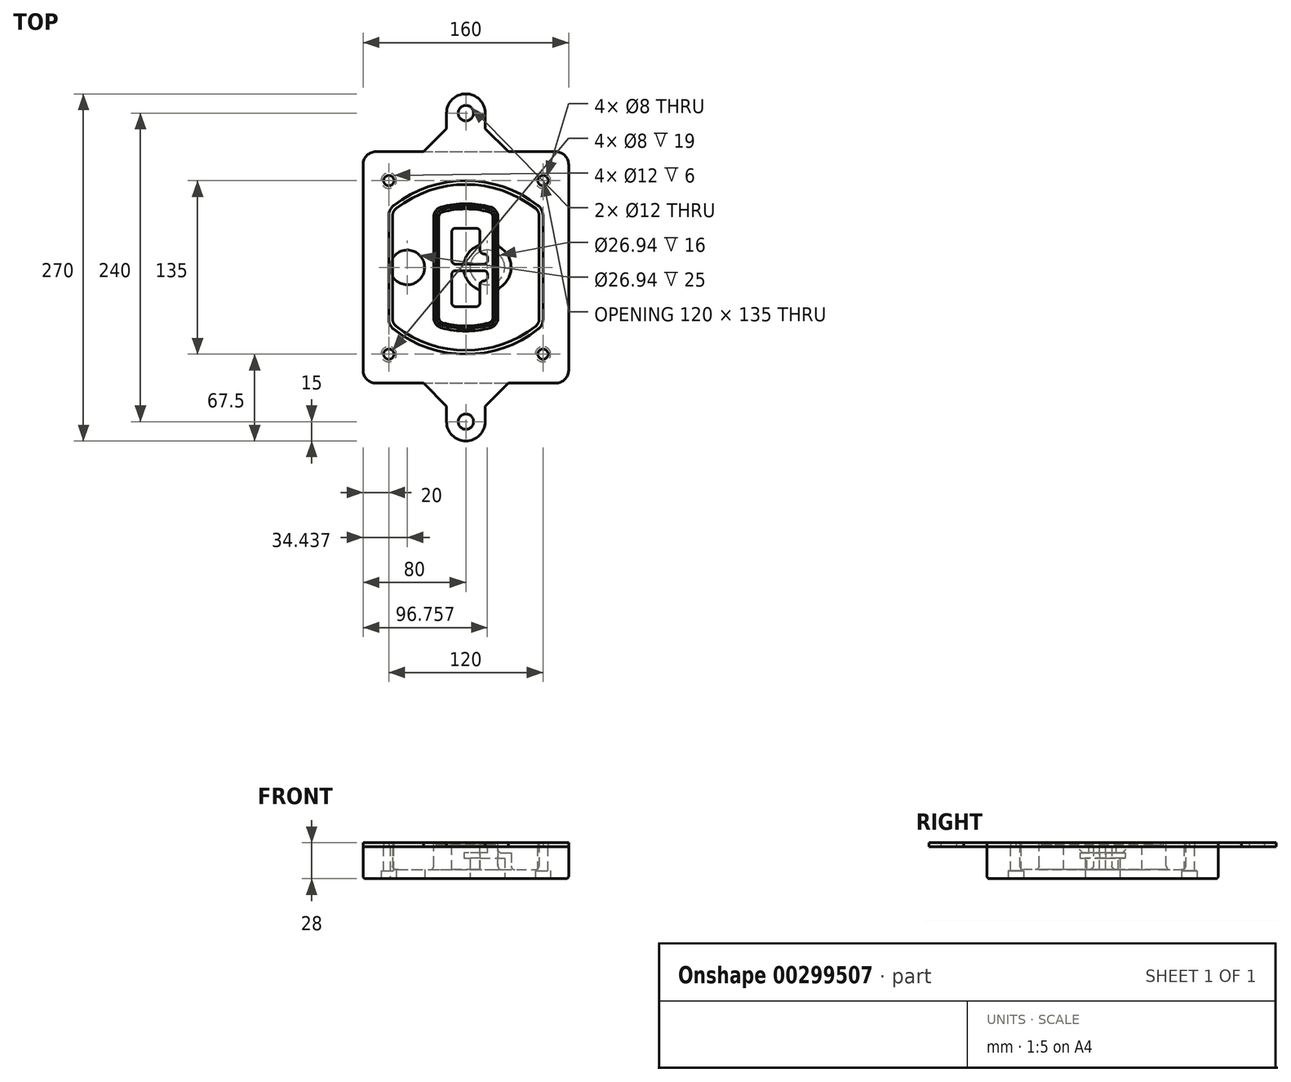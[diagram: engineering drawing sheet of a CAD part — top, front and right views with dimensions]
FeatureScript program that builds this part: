
annotation { "Feature Type Name" : "Feature", "Feature Type Description" : "" }
export const myFeature = defineFeature(function(context is Context, id is Id, definition is map)
    precondition{}
    {
        {
            var Q0;
            Q0=qCreatedBy(makeId("Top.planeOp"),FACE);
            var sketch = newSketch(context, id + "F0", { "sketchPlane" : qUnion([Q0])});
            skPoint(sketch, "E0.rect.middle", {"position": v(0, 0) * mm});
            skLineSegment(sketch, "E1.bottom", {"start": v(-70, -90) * mm, "end": v(70, -90) * mm});
            skLineSegment(sketch, "E1.top", {"start": v(-70, 90) * mm, "end": v(70, 90) * mm});
            skLineSegment(sketch, "E1.left", {"start": v(-80, -80) * mm, "end": v(-80, 80) * mm});
            skLineSegment(sketch, "E1.right", {"start": v(80, -80) * mm, "end": v(80, 80) * mm});
            skLineSegment(sketch, "E2", {"start": v(-80, 90) * mm, "end": v(80, -90) * mm, "construction": true});
            skLineSegment(sketch, "E3", {"start": v(80, 90) * mm, "end": v(-80, -90) * mm, "construction": true});
            skCircle(sketch, "E4", {"center": v(-60, 67.5) * mm, "radius": 4 * mm});
            skCircle(sketch, "E5", {"center": v(60, 67.5) * mm, "radius": 4 * mm});
            skCircle(sketch, "E6", {"center": v(60, -67.5) * mm, "radius": 4 * mm});
            skCircle(sketch, "E7", {"center": v(-60, -67.5) * mm, "radius": 4 * mm});
            skLineSegment(sketch, "E8", {"start": v(-60, 67.5) * mm, "end": v(60, 67.5) * mm, "construction": true});
            skLineSegment(sketch, "E9", {"start": v(60, 67.5) * mm, "end": v(60, -67.5) * mm, "construction": true});
            skLineSegment(sketch, "E10", {"start": v(60, -67.5) * mm, "end": v(-60, -67.5) * mm, "construction": true});
            skLineSegment(sketch, "E11", {"start": v(-60, -67.5) * mm, "end": v(-60, 67.5) * mm, "construction": true});
            skLineSegment(sketch, "E12", {"start": v(-60, 40.3) * mm, "end": v(-60, -40.3) * mm});
            skLineSegment(sketch, "E13", {"start": v(60, 40.3) * mm, "end": v(60, -40.3) * mm});
            skArc(sketch, "E14", {"start": v(56.15, 48.18) * mm, "mid": v(0, 67.5) * mm, "end": v(-56.15, 48.18) * mm});
            skArc(sketch, "E15", {"start": v(-56.15, -48.18) * mm, "mid": v(0, -67.5) * mm, "end": v(56.15, -48.18) * mm});
            skLineSegment(sketch, "E16", {"start": v(-60, 0) * mm, "end": v(60, 0) * mm, "construction": true});
            skPoint(sketch, "E17.visualSharp", {"position": v(-60, -45) * mm});
            skArc(sketch, "E17.filletArc", {"start": v(-60, -40.3) * mm, "mid": v(-58.99, -44.68) * mm, "end": v(-56.15, -48.18) * mm});
            skPoint(sketch, "E18.visualSharp", {"position": v(-60, 45) * mm});
            skArc(sketch, "E18.filletArc", {"start": v(-56.15, 48.18) * mm, "mid": v(-58.99, 44.68) * mm, "end": v(-60, 40.3) * mm});
            skPoint(sketch, "E19.visualSharp", {"position": v(60, 45) * mm});
            skArc(sketch, "E19.filletArc", {"start": v(60, 40.3) * mm, "mid": v(58.99, 44.68) * mm, "end": v(56.15, 48.18) * mm});
            skPoint(sketch, "E20.visualSharp", {"position": v(60, -45) * mm});
            skArc(sketch, "E20.filletArc", {"start": v(56.15, -48.18) * mm, "mid": v(58.99, -44.68) * mm, "end": v(60, -40.3) * mm});
            skPoint(sketch, "E21.visualSharp", {"position": v(-80, 90) * mm});
            skArc(sketch, "E21.filletArc", {"start": v(-70, 90) * mm, "mid": v(-77.07, 87.07) * mm, "end": v(-80, 80) * mm});
            skPoint(sketch, "E22.visualSharp", {"position": v(80, 90) * mm});
            skArc(sketch, "E22.filletArc", {"start": v(80, 80) * mm, "mid": v(77.07, 87.07) * mm, "end": v(70, 90) * mm});
            skPoint(sketch, "E23.visualSharp", {"position": v(80, -90) * mm});
            skArc(sketch, "E23.filletArc", {"start": v(70, -90) * mm, "mid": v(77.07, -87.07) * mm, "end": v(80, -80) * mm});
            skPoint(sketch, "E24.visualSharp", {"position": v(-80, -90) * mm});
            skArc(sketch, "E24.filletArc", {"start": v(-80, -80) * mm, "mid": v(-77.07, -87.07) * mm, "end": v(-70, -90) * mm});
            skArc(sketch, "E25.0", {"start": v(57, 40.3) * mm, "mid": v(56.3, 43.36) * mm, "end": v(54.3, 45.81) * mm});
            skLineSegment(sketch, "E25.1", {"start": v(57, 40.3) * mm, "end": v(57, -40.3) * mm});
            skArc(sketch, "E25.2", {"start": v(54.3, -45.81) * mm, "mid": v(56.3, -43.36) * mm, "end": v(57, -40.3) * mm});
            skArc(sketch, "E25.3", {"start": v(-54.3, -45.81) * mm, "mid": v(0, -64.5) * mm, "end": v(54.3, -45.81) * mm});
            skArc(sketch, "E25.4", {"start": v(-57, -40.3) * mm, "mid": v(-56.3, -43.36) * mm, "end": v(-54.3, -45.81) * mm});
            skArc(sketch, "E25.5", {"start": v(54.3, 45.81) * mm, "mid": v(0, 64.5) * mm, "end": v(-54.3, 45.81) * mm});
            skLineSegment(sketch, "E25.6", {"start": v(-57, 40.3) * mm, "end": v(-57, -40.3) * mm});
            skArc(sketch, "E25.7", {"start": v(-54.3, 45.81) * mm, "mid": v(-56.3, 43.36) * mm, "end": v(-57, 40.3) * mm});
            skArc(sketch, "E26.0", {"start": v(-58.62, 51.33) * mm, "mid": v(-62.58, 46.43) * mm, "end": v(-64, 40.3) * mm});
            skArc(sketch, "E26.1", {"start": v(58.62, 51.33) * mm, "mid": v(0, 71.5) * mm, "end": v(-58.62, 51.33) * mm});
            skArc(sketch, "E26.2", {"start": v(64, 40.3) * mm, "mid": v(62.58, 46.43) * mm, "end": v(58.62, 51.33) * mm});
            skLineSegment(sketch, "E26.3", {"start": v(64, 40.3) * mm, "end": v(64, -40.3) * mm});
            skArc(sketch, "E26.4", {"start": v(58.62, -51.33) * mm, "mid": v(62.58, -46.43) * mm, "end": v(64, -40.3) * mm});
            skLineSegment(sketch, "E26.5", {"start": v(-64, 40.3) * mm, "end": v(-64, -40.3) * mm});
            skArc(sketch, "E26.6", {"start": v(-58.62, -51.33) * mm, "mid": v(0, -71.5) * mm, "end": v(58.62, -51.33) * mm});
            skArc(sketch, "E26.7", {"start": v(-64, -40.3) * mm, "mid": v(-62.58, -46.43) * mm, "end": v(-58.62, -51.33) * mm});
            skSolve(sketch);
        }
        {
            var Q0;
            Q0=makeQuery(id+"F0.imprint","IMPRINT",FACE,{"disambiguationData":[TD([[makeQuery(id+"F0.imprint","IMPRINT",EDGE,{"derivedFrom":sQuery(id+"F0.wireOp",EDGE,"E1.bottom")}),1.0]])]});
            var Q1;
            Q1=makeQuery(id+"F0.imprint","IMPRINT",FACE,{"disambiguationData":[TD([[makeQuery(id+"F0.imprint","IMPRINT",EDGE,{"derivedFrom":sQuery(id+"F0.wireOp",EDGE,"E12")}),1.0]])]});
            var Q2;
            Q2=makeQuery(id+"F0.imprint","IMPRINT",FACE,{"disambiguationData":[TD([[makeQuery(id+"F0.imprint","IMPRINT",EDGE,{"derivedFrom":sQuery(id+"F0.wireOp",EDGE,"E25.0")}),1.0]])]});
            var Q3;
            Q3=makeQuery(id+"F0.imprint","IMPRINT",FACE,{"disambiguationData":[TD([[makeQuery(id+"F0.imprint","IMPRINT",EDGE,{"derivedFrom":sQuery(id+"F0.wireOp",EDGE,"E12")}),-1.0]])]});
            extrude(context, id + "F1", {"entities" : qUnion([Q0, Q1, Q2, Q3]), "oppositeDirection" : true, "depth" : 25 * mm});
        }
        {
            var Q0;
            Q0=makeQuery(id+"F0.imprint","IMPRINT",FACE,{"disambiguationData":[TD([[makeQuery(id+"F0.imprint","IMPRINT",EDGE,{"derivedFrom":sQuery(id+"F0.wireOp",EDGE,"E12")}),1.0]])]});
            extrude(context, id + "F2", {"entities" : qUnion([Q0]), "operationType" : NewBodyOperationType.ADD, "depth" : 3 * mm});
        }
        {
            var Q0;
            Q0=makeQuery(id+"F0.imprint","IMPRINT",FACE,{"disambiguationData":[TD([[makeQuery(id+"F0.imprint","IMPRINT",EDGE,{"derivedFrom":sQuery(id+"F0.wireOp",EDGE,"E25.0")}),1.0]])]});
            extrude(context, id + "F3", {"entities" : qUnion([Q0]), "operationType" : NewBodyOperationType.REMOVE, "oppositeDirection" : true, "depth" : 18 * mm});
        }
        {
            var Q0;
            Q0=makeQuery(id+"F2.opExtrude","CAP_FACE",FACE,{"disambiguationData":[OSD([sQuery(id+"F0.wireOp",EDGE,"E12"),sQuery(id+"F0.wireOp",EDGE,"E13"),sQuery(id+"F0.wireOp",EDGE,"E14"),sQuery(id+"F0.wireOp",EDGE,"E15"),sQuery(id+"F0.wireOp",EDGE,"E17.filletArc"),sQuery(id+"F0.wireOp",EDGE,"E18.filletArc"),sQuery(id+"F0.wireOp",EDGE,"E19.filletArc"),sQuery(id+"F0.wireOp",EDGE,"E20.filletArc"),sQuery(id+"F0.wireOp",EDGE,"E25.0"),sQuery(id+"F0.wireOp",EDGE,"E25.1"),sQuery(id+"F0.wireOp",EDGE,"E25.2"),sQuery(id+"F0.wireOp",EDGE,"E25.3"),sQuery(id+"F0.wireOp",EDGE,"E25.4"),sQuery(id+"F0.wireOp",EDGE,"E25.5"),sQuery(id+"F0.wireOp",EDGE,"E25.6"),sQuery(id+"F0.wireOp",EDGE,"E25.7")])],"isStart":false});
            var sketch = newSketch(context, id + "F4", { "sketchPlane" : qUnion([Q0])});
            skArc(sketch, "E27.0", {"start": v(-19.08, -46.97) * mm, "mid": v(0, -49.5) * mm, "end": v(19.08, -46.97) * mm});
            skArc(sketch, "E28.0", {"start": v(19.08, 46.97) * mm, "mid": v(0, 49.5) * mm, "end": v(-19.08, 46.97) * mm});
            skLineSegment(sketch, "E29", {"start": v(-25, 39.25) * mm, "end": v(-25, -39.25) * mm});
            skLineSegment(sketch, "E30", {"start": v(25, 39.25) * mm, "end": v(25, -39.25) * mm});
            skLineSegment(sketch, "E31", {"start": v(-25, 45.1) * mm, "end": v(25, 45.1) * mm, "construction": true});
            skLineSegment(sketch, "E32", {"start": v(-25, -45.1) * mm, "end": v(25, -45.1) * mm, "construction": true});
            skPoint(sketch, "E33.visualSharp", {"position": v(-25, 45.1) * mm});
            skArc(sketch, "E33.filletArc", {"start": v(-19.08, 46.97) * mm, "mid": v(-23.35, 44.11) * mm, "end": v(-25, 39.25) * mm});
            skPoint(sketch, "E34.visualSharp", {"position": v(25, 45.1) * mm});
            skArc(sketch, "E34.filletArc", {"start": v(25, 39.25) * mm, "mid": v(23.35, 44.11) * mm, "end": v(19.08, 46.97) * mm});
            skPoint(sketch, "E35.visualSharp", {"position": v(25, -45.1) * mm});
            skArc(sketch, "E35.filletArc", {"start": v(19.08, -46.97) * mm, "mid": v(23.35, -44.11) * mm, "end": v(25, -39.25) * mm});
            skPoint(sketch, "E36.visualSharp", {"position": v(-25, -45.1) * mm});
            skArc(sketch, "E36.filletArc", {"start": v(-25, -39.25) * mm, "mid": v(-23.35, -44.11) * mm, "end": v(-19.08, -46.97) * mm});
            skArc(sketch, "E37.0", {"start": v(54.3, 45.81) * mm, "mid": v(0, 64.5) * mm, "end": v(-54.3, 45.81) * mm});
            skArc(sketch, "E37.1", {"start": v(-54.3, 45.81) * mm, "mid": v(-56.3, 43.36) * mm, "end": v(-57, 40.3) * mm});
            skLineSegment(sketch, "E37.2", {"start": v(-57, 40.3) * mm, "end": v(-57, -40.3) * mm});
            skArc(sketch, "E37.3", {"start": v(-57, -40.3) * mm, "mid": v(-56.3, -43.36) * mm, "end": v(-54.3, -45.81) * mm});
            skArc(sketch, "E37.4", {"start": v(-54.3, -45.81) * mm, "mid": v(0, -64.5) * mm, "end": v(54.3, -45.81) * mm});
            skArc(sketch, "E37.5", {"start": v(54.3, -45.81) * mm, "mid": v(56.3, -43.36) * mm, "end": v(57, -40.3) * mm});
            skLineSegment(sketch, "E37.6", {"start": v(57, 40.3) * mm, "end": v(57, -40.3) * mm});
            skArc(sketch, "E37.7", {"start": v(57, 40.3) * mm, "mid": v(56.3, 43.36) * mm, "end": v(54.3, 45.81) * mm});
            skLineSegment(sketch, "E38.0", {"start": v(23, 39.25) * mm, "end": v(23, -39.25) * mm});
            skArc(sketch, "E38.1", {"start": v(18.56, -45.04) * mm, "mid": v(21.76, -42.9) * mm, "end": v(23, -39.25) * mm});
            skArc(sketch, "E38.2", {"start": v(-18.56, -45.04) * mm, "mid": v(0, -47.5) * mm, "end": v(18.56, -45.04) * mm});
            skArc(sketch, "E38.3", {"start": v(-23, -39.25) * mm, "mid": v(-21.76, -42.9) * mm, "end": v(-18.56, -45.04) * mm});
            skLineSegment(sketch, "E38.4", {"start": v(-23, 39.25) * mm, "end": v(-23, -39.25) * mm});
            skArc(sketch, "E38.5", {"start": v(23, 39.25) * mm, "mid": v(21.76, 42.9) * mm, "end": v(18.56, 45.04) * mm});
            skArc(sketch, "E38.6", {"start": v(-18.56, 45.04) * mm, "mid": v(-21.76, 42.9) * mm, "end": v(-23, 39.25) * mm});
            skArc(sketch, "E38.7", {"start": v(18.56, 45.04) * mm, "mid": v(0, 47.5) * mm, "end": v(-18.56, 45.04) * mm});
            skArc(sketch, "E39.0", {"start": v(21, 39.25) * mm, "mid": v(20.18, 41.68) * mm, "end": v(18.04, 43.1) * mm});
            skLineSegment(sketch, "E39.1", {"start": v(21, 39.25) * mm, "end": v(21, -39.25) * mm});
            skArc(sketch, "E39.2", {"start": v(18.04, -43.1) * mm, "mid": v(20.18, -41.68) * mm, "end": v(21, -39.25) * mm});
            skArc(sketch, "E39.3", {"start": v(-18.04, -43.1) * mm, "mid": v(0, -45.5) * mm, "end": v(18.04, -43.1) * mm});
            skArc(sketch, "E39.4", {"start": v(-21, -39.25) * mm, "mid": v(-20.18, -41.68) * mm, "end": v(-18.04, -43.1) * mm});
            skArc(sketch, "E39.5", {"start": v(18.04, 43.1) * mm, "mid": v(0, 45.5) * mm, "end": v(-18.04, 43.1) * mm});
            skLineSegment(sketch, "E39.6", {"start": v(-21, 39.25) * mm, "end": v(-21, -39.25) * mm});
            skArc(sketch, "E39.7", {"start": v(-18.04, 43.1) * mm, "mid": v(-20.18, 41.68) * mm, "end": v(-21, 39.25) * mm});
            skLineSegment(sketch, "E40", {"start": v(-25, 0) * mm, "end": v(25, 0) * mm, "construction": true});
            skLineSegment(sketch, "E41", {"start": v(-11, 5.5) * mm, "end": v(-11, 27.5) * mm});
            skLineSegment(sketch, "E42", {"start": v(-8, 30.5) * mm, "end": v(8, 30.5) * mm});
            skLineSegment(sketch, "E43", {"start": v(11, 27.5) * mm, "end": v(11, 13.5) * mm});
            skLineSegment(sketch, "E44", {"start": v(14, 10.5) * mm, "end": v(14, 10.5) * mm});
            skLineSegment(sketch, "E45", {"start": v(17, 7.5) * mm, "end": v(17, 5.5) * mm});
            skLineSegment(sketch, "E46", {"start": v(14, 2.5) * mm, "end": v(-8, 2.5) * mm});
            skPoint(sketch, "E47.visualSharp", {"position": v(-11, 30.5) * mm});
            skArc(sketch, "E47.filletArc", {"start": v(-8, 30.5) * mm, "mid": v(-10.12, 29.62) * mm, "end": v(-11, 27.5) * mm});
            skPoint(sketch, "E48.visualSharp", {"position": v(11, 30.5) * mm});
            skArc(sketch, "E48.filletArc", {"start": v(11, 27.5) * mm, "mid": v(10.12, 29.62) * mm, "end": v(8, 30.5) * mm});
            skPoint(sketch, "E49.visualSharp", {"position": v(11, 10.5) * mm});
            skArc(sketch, "E49.filletArc", {"start": v(11, 13.5) * mm, "mid": v(11.88, 11.38) * mm, "end": v(14, 10.5) * mm});
            skPoint(sketch, "E50.visualSharp", {"position": v(17, 10.5) * mm});
            skArc(sketch, "E50.filletArc", {"start": v(17, 7.5) * mm, "mid": v(16.12, 9.62) * mm, "end": v(14, 10.5) * mm});
            skPoint(sketch, "E51.visualSharp", {"position": v(17, 2.5) * mm});
            skArc(sketch, "E51.filletArc", {"start": v(14, 2.5) * mm, "mid": v(16.12, 3.38) * mm, "end": v(17, 5.5) * mm});
            skPoint(sketch, "E52.visualSharp", {"position": v(-11, 2.5) * mm});
            skArc(sketch, "E52.filletArc", {"start": v(-11, 5.5) * mm, "mid": v(-10.12, 3.38) * mm, "end": v(-8, 2.5) * mm});
            skLineSegment(sketch, "E53.0.MirrorCS", {"start": v(14, -2.5) * mm, "end": v(-8, -2.5) * mm});
            skArc(sketch, "E54.0.MirrorCS", {"start": v(-11, -5.5) * mm, "mid": v(-10.12, -3.38) * mm, "end": v(-8, -2.5) * mm});
            skLineSegment(sketch, "E55.0.MirrorCS", {"start": v(-11, -5.5) * mm, "end": v(-11, -27.5) * mm});
            skArc(sketch, "E56.0.MirrorCS", {"start": v(-8, -30.5) * mm, "mid": v(-10.12, -29.62) * mm, "end": v(-11, -27.5) * mm});
            skLineSegment(sketch, "E57.0.MirrorCS", {"start": v(-8, -30.5) * mm, "end": v(8, -30.5) * mm});
            skArc(sketch, "E58.0.MirrorCS", {"start": v(11, -27.5) * mm, "mid": v(10.12, -29.62) * mm, "end": v(8, -30.5) * mm});
            skLineSegment(sketch, "E59.0.MirrorCS", {"start": v(11, -27.5) * mm, "end": v(11, -13.5) * mm});
            skArc(sketch, "E60.0.MirrorCS", {"start": v(11, -13.5) * mm, "mid": v(11.88, -11.38) * mm, "end": v(14, -10.5) * mm});
            skArc(sketch, "E61.0.MirrorCS", {"start": v(17, -7.5) * mm, "mid": v(16.12, -9.62) * mm, "end": v(14, -10.5) * mm});
            skLineSegment(sketch, "E62.0.MirrorCS", {"start": v(17, -7.5) * mm, "end": v(17, -5.5) * mm});
            skArc(sketch, "E63.0.MirrorCS", {"start": v(14, -2.5) * mm, "mid": v(16.12, -3.38) * mm, "end": v(17, -5.5) * mm});
            skSolve(sketch);
        }
        {
            var Q0;
            Q0=makeQuery(id+"F4.imprint","IMPRINT",FACE,{"disambiguationData":[TD([[makeQuery(id+"F4.imprint","IMPRINT",EDGE,{"derivedFrom":sQuery(id+"F4.wireOp",EDGE,"E27.0")}),1.0]])]});
            var Q1;
            Q1=makeQuery(id+"F4.imprint","IMPRINT",FACE,{"disambiguationData":[TD([[makeQuery(id+"F4.imprint","IMPRINT",EDGE,{"derivedFrom":sQuery(id+"F4.wireOp",EDGE,"E38.0")}),-1.0]])]});
            var Q2;
            Q2=makeQuery(id+"F4.imprint","IMPRINT",FACE,{"disambiguationData":[TD([[makeQuery(id+"F4.imprint","IMPRINT",EDGE,{"derivedFrom":sQuery(id+"F4.wireOp",EDGE,"E39.0")}),1.0]])]});
            extrude(context, id + "F5", {"entities" : qUnion([Q0, Q1, Q2]), "operationType" : NewBodyOperationType.ADD, "endBound" : BoundingType.UP_TO_NEXT, "oppositeDirection" : true, "depth" : 25 * mm});
        }
        {
            var Q0;
            Q0=makeQuery(id+"F4.imprint","IMPRINT",FACE,{"disambiguationData":[TD([[makeQuery(id+"F4.imprint","IMPRINT",EDGE,{"derivedFrom":sQuery(id+"F4.wireOp",EDGE,"E38.0")}),-1.0]])]});
            extrude(context, id + "F6", {"entities" : qUnion([Q0]), "operationType" : NewBodyOperationType.REMOVE, "oppositeDirection" : true, "depth" : 2 * mm});
        }
        {
            var Q0;
            Q0=makeQuery(id+"F1.opExtrude","CAP_FACE",FACE,{"disambiguationData":[OSD([sQuery(id+"F0.wireOp",EDGE,"E1.bottom"),sQuery(id+"F0.wireOp",EDGE,"E1.top"),sQuery(id+"F0.wireOp",EDGE,"E1.left"),sQuery(id+"F0.wireOp",EDGE,"E1.right"),sQuery(id+"F0.wireOp",EDGE,"E4"),sQuery(id+"F0.wireOp",EDGE,"E5"),sQuery(id+"F0.wireOp",EDGE,"E6"),sQuery(id+"F0.wireOp",EDGE,"E7"),sQuery(id+"F0.wireOp",EDGE,"E21.filletArc"),sQuery(id+"F0.wireOp",EDGE,"E22.filletArc"),sQuery(id+"F0.wireOp",EDGE,"E23.filletArc"),sQuery(id+"F0.wireOp",EDGE,"E24.filletArc")])],"isStart":false});
            var sketch = newSketch(context, id + "F7", { "sketchPlane" : qUnion([Q0])});
            skCircle(sketch, "E64", {"center": v(16.76, 0) * mm, "radius": 13.47 * mm});
            skCircle(sketch, "E65", {"center": v(-45.56, 0) * mm, "radius": 13.47 * mm});
            skLineSegment(sketch, "E66", {"start": v(80, 0) * mm, "end": v(-80, 0) * mm});
            skCircle(sketch, "E67", {"center": v(16.76, 0) * mm, "radius": 18.47 * mm});
            skCircle(sketch, "E68", {"center": v(60, -67.5) * mm, "radius": 6 * mm});
            skCircle(sketch, "E69", {"center": v(-60, -67.5) * mm, "radius": 6 * mm});
            skCircle(sketch, "E70", {"center": v(-60, 67.5) * mm, "radius": 6 * mm});
            skCircle(sketch, "E71", {"center": v(60, 67.5) * mm, "radius": 6 * mm});
            skSolve(sketch);
        }
        {
            var Q0;
            {var subQ1=sQuery(id+"F7.wireOp",EDGE,"E66");var subQ4=sQuery(id+"F7.wireOp",EDGE,"E64");var subQ6=makeQuery(id+"F7.imprint","INTERSECT",VERTEX,{"disambiguationData":[OD(0.0)],"derivedFrom":[subQ4,subQ1]});Q0=makeQuery(id+"F7.imprint","IMPRINT",FACE,{"disambiguationData":[TD([[makeQuery(id+"F7.imprint","IMPRINT",EDGE,{"disambiguationData":[TD([[subQ6,-1.0]])],"derivedFrom":subQ4}),-1.0]])]});}
            var Q1;
            {var subQ0=sQuery(id+"F7.wireOp",EDGE,"E66");var subQ1=sQuery(id+"F7.wireOp",EDGE,"E64");var subQ3=makeQuery(id+"F7.imprint","INTERSECT",VERTEX,{"disambiguationData":[OD(0.0)],"derivedFrom":[subQ1,subQ0]});Q1=makeQuery(id+"F7.imprint","IMPRINT",FACE,{"disambiguationData":[TD([[makeQuery(id+"F7.imprint","IMPRINT",EDGE,{"disambiguationData":[TD([[subQ3,-1.0]])],"derivedFrom":subQ1}),1.0]])]});}
            var Q2;
            {var subQ0=sQuery(id+"F7.wireOp",EDGE,"E66");var subQ1=sQuery(id+"F7.wireOp",EDGE,"E64");var subQ3=makeQuery(id+"F7.imprint","INTERSECT",VERTEX,{"disambiguationData":[OD(0.0)],"derivedFrom":[subQ1,subQ0]});Q2=makeQuery(id+"F7.imprint","IMPRINT",FACE,{"disambiguationData":[TD([[makeQuery(id+"F7.imprint","IMPRINT",EDGE,{"disambiguationData":[TD([[subQ3,1.0]])],"derivedFrom":subQ1}),1.0]])]});}
            var Q3;
            {var subQ1=sQuery(id+"F7.wireOp",EDGE,"E66");var subQ4=sQuery(id+"F7.wireOp",EDGE,"E64");var subQ6=makeQuery(id+"F7.imprint","INTERSECT",VERTEX,{"disambiguationData":[OD(0.0)],"derivedFrom":[subQ4,subQ1]});Q3=makeQuery(id+"F7.imprint","IMPRINT",FACE,{"disambiguationData":[TD([[makeQuery(id+"F7.imprint","IMPRINT",EDGE,{"disambiguationData":[TD([[subQ6,1.0]])],"derivedFrom":subQ4}),-1.0]])]});}
            extrude(context, id + "F8", {"entities" : qUnion([Q0, Q1, Q2, Q3]), "operationType" : NewBodyOperationType.ADD, "oppositeDirection" : true, "depth" : 20 * mm});
        }
        {
            var Q0;
            {var subQ0=sQuery(id+"F7.wireOp",EDGE,"E66");var subQ1=sQuery(id+"F7.wireOp",EDGE,"E64");var subQ3=makeQuery(id+"F7.imprint","INTERSECT",VERTEX,{"disambiguationData":[OD(0.0)],"derivedFrom":[subQ1,subQ0]});Q0=makeQuery(id+"F7.imprint","IMPRINT",FACE,{"disambiguationData":[TD([[makeQuery(id+"F7.imprint","IMPRINT",EDGE,{"disambiguationData":[TD([[subQ3,-1.0]])],"derivedFrom":subQ1}),1.0]])]});}
            var Q1;
            {var subQ0=sQuery(id+"F7.wireOp",EDGE,"E66");var subQ1=sQuery(id+"F7.wireOp",EDGE,"E64");var subQ3=makeQuery(id+"F7.imprint","INTERSECT",VERTEX,{"disambiguationData":[OD(0.0)],"derivedFrom":[subQ1,subQ0]});Q1=makeQuery(id+"F7.imprint","IMPRINT",FACE,{"disambiguationData":[TD([[makeQuery(id+"F7.imprint","IMPRINT",EDGE,{"disambiguationData":[TD([[subQ3,1.0]])],"derivedFrom":subQ1}),1.0]])]});}
            extrude(context, id + "F9", {"entities" : qUnion([Q0, Q1]), "operationType" : NewBodyOperationType.REMOVE, "oppositeDirection" : true, "depth" : 16 * mm});
        }
        {
            var Q0;
            {var subQ0=sQuery(id+"F7.wireOp",EDGE,"E66");var subQ1=sQuery(id+"F7.wireOp",EDGE,"E65");var subQ3=makeQuery(id+"F7.imprint","INTERSECT",VERTEX,{"disambiguationData":[OD(0.0)],"derivedFrom":[subQ1,subQ0]});Q0=makeQuery(id+"F7.imprint","IMPRINT",FACE,{"disambiguationData":[TD([[makeQuery(id+"F7.imprint","IMPRINT",EDGE,{"disambiguationData":[TD([[subQ3,-1.0]])],"derivedFrom":subQ1}),1.0]])]});}
            var Q1;
            {var subQ0=sQuery(id+"F7.wireOp",EDGE,"E66");var subQ1=sQuery(id+"F7.wireOp",EDGE,"E65");var subQ3=makeQuery(id+"F7.imprint","INTERSECT",VERTEX,{"disambiguationData":[OD(0.0)],"derivedFrom":[subQ1,subQ0]});Q1=makeQuery(id+"F7.imprint","IMPRINT",FACE,{"disambiguationData":[TD([[makeQuery(id+"F7.imprint","IMPRINT",EDGE,{"disambiguationData":[TD([[subQ3,1.0]])],"derivedFrom":subQ1}),1.0]])]});}
            extrude(context, id + "F10", {"entities" : qUnion([Q0, Q1]), "operationType" : NewBodyOperationType.REMOVE, "oppositeDirection" : true, "depth" : 25 * mm});
        }
        {
            var Q0;
            Q0=makeQuery(id+"F7.imprint","IMPRINT",FACE,{"disambiguationData":[TD([[makeQuery(id+"F7.imprint","IMPRINT",EDGE,{"derivedFrom":sQuery(id+"F7.wireOp",EDGE,"E68")}),1.0]])]});
            var Q1;
            Q1=makeQuery(id+"F7.imprint","IMPRINT",FACE,{"disambiguationData":[TD([[makeQuery(id+"F7.imprint","IMPRINT",EDGE,{"derivedFrom":makeQuery(id+"F1.opExtrude","CAP_EDGE",EDGE,{"disambiguationData":[OSD([sQuery(id+"F0.wireOp",EDGE,"E5")])],"isStart":false})}),-1.0]])]});
            var Q2;
            Q2=makeQuery(id+"F7.imprint","IMPRINT",FACE,{"disambiguationData":[TD([[makeQuery(id+"F7.imprint","IMPRINT",EDGE,{"derivedFrom":sQuery(id+"F7.wireOp",EDGE,"E69")}),1.0]])]});
            var Q3;
            Q3=makeQuery(id+"F7.imprint","IMPRINT",FACE,{"disambiguationData":[TD([[makeQuery(id+"F7.imprint","IMPRINT",EDGE,{"derivedFrom":makeQuery(id+"F1.opExtrude","CAP_EDGE",EDGE,{"disambiguationData":[OSD([sQuery(id+"F0.wireOp",EDGE,"E4")])],"isStart":false})}),-1.0]])]});
            var Q4;
            Q4=makeQuery(id+"F7.imprint","IMPRINT",FACE,{"disambiguationData":[TD([[makeQuery(id+"F7.imprint","IMPRINT",EDGE,{"derivedFrom":sQuery(id+"F7.wireOp",EDGE,"E70")}),1.0]])]});
            var Q5;
            Q5=makeQuery(id+"F7.imprint","IMPRINT",FACE,{"disambiguationData":[TD([[makeQuery(id+"F7.imprint","IMPRINT",EDGE,{"derivedFrom":makeQuery(id+"F1.opExtrude","CAP_EDGE",EDGE,{"disambiguationData":[OSD([sQuery(id+"F0.wireOp",EDGE,"E7")])],"isStart":false})}),-1.0]])]});
            var Q6;
            Q6=makeQuery(id+"F7.imprint","IMPRINT",FACE,{"disambiguationData":[TD([[makeQuery(id+"F7.imprint","IMPRINT",EDGE,{"derivedFrom":sQuery(id+"F7.wireOp",EDGE,"E71")}),1.0]])]});
            var Q7;
            Q7=makeQuery(id+"F7.imprint","IMPRINT",FACE,{"disambiguationData":[TD([[makeQuery(id+"F7.imprint","IMPRINT",EDGE,{"derivedFrom":makeQuery(id+"F1.opExtrude","CAP_EDGE",EDGE,{"disambiguationData":[OSD([sQuery(id+"F0.wireOp",EDGE,"E6")])],"isStart":false})}),-1.0]])]});
            extrude(context, id + "F11", {"entities" : qUnion([Q0, Q1, Q2, Q3, Q4, Q5, Q6, Q7]), "operationType" : NewBodyOperationType.REMOVE, "oppositeDirection" : true, "depth" : 6 * mm});
        }
        {
            var Q0;
            Q0=makeQuery(id+"F9.boolean.opBoolean","COPY",FACE,{"derivedFrom":makeQuery(id+"F9.opExtrude","CAP_FACE",FACE,{"disambiguationData":[OSD([sQuery(id+"F7.wireOp",EDGE,"E64")])],"isStart":false})});
            var sketch = newSketch(context, id + "F12", { "sketchPlane" : qUnion([Q0])});
            skArc(sketch, "E72.0", {"start": v(11, 17.55) * mm, "mid": v(2.57, 11.82) * mm, "end": v(-1.54, 2.5) * mm});
            skArc(sketch, "E72.1", {"start": v(-1.54, -2.5) * mm, "mid": v(2.57, -11.82) * mm, "end": v(11, -17.55) * mm});
            skLineSegment(sketch, "E73", {"start": v(-1.54, -2.5) * mm, "end": v(14, -2.5) * mm});
            skLineSegment(sketch, "E74.0", {"start": v(14, 2.5) * mm, "end": v(-1.54, 2.5) * mm});
            skArc(sketch, "E74.1", {"start": v(14, 2.5) * mm, "mid": v(16.12, 3.38) * mm, "end": v(17, 5.5) * mm});
            skLineSegment(sketch, "E74.2", {"start": v(17, 7.5) * mm, "end": v(17, 5.5) * mm});
            skArc(sketch, "E74.3", {"start": v(17, 7.5) * mm, "mid": v(16.12, 9.62) * mm, "end": v(14, 10.5) * mm});
            skArc(sketch, "E74.4", {"start": v(11, 13.5) * mm, "mid": v(11.88, 11.38) * mm, "end": v(14, 10.5) * mm});
            skLineSegment(sketch, "E74.5", {"start": v(11, 17.55) * mm, "end": v(11, 13.5) * mm});
            skLineSegment(sketch, "E74.7", {"start": v(14, -2.5) * mm, "end": v(-1.54, -2.5) * mm});
            skArc(sketch, "E74.8", {"start": v(14, -2.5) * mm, "mid": v(16.12, -3.38) * mm, "end": v(17, -5.5) * mm});
            skLineSegment(sketch, "E74.9", {"start": v(17, -7.5) * mm, "end": v(17, -5.5) * mm});
            skArc(sketch, "E74.10", {"start": v(17, -7.5) * mm, "mid": v(16.12, -9.62) * mm, "end": v(14, -10.5) * mm});
            skArc(sketch, "E74.11", {"start": v(11, -13.5) * mm, "mid": v(11.88, -11.38) * mm, "end": v(14, -10.5) * mm});
            skLineSegment(sketch, "E74.12", {"start": v(11, -17.55) * mm, "end": v(11, -13.5) * mm});
            skPoint(sketch, "E75.orphan", {"position": v(11, -27.5) * mm});
            skPoint(sketch, "E76.orphan", {"position": v(-8, -2.5) * mm});
            skPoint(sketch, "E77.orphan", {"position": v(-8, 2.5) * mm});
            skPoint(sketch, "E78.orphan", {"position": v(11, 27.5) * mm});
            skSolve(sketch);
        }
        {
            var Q0;
            {var subQ7=sQuery(id+"F12.wireOp",EDGE,"E72.0");var subQ14=sQuery(id+"F12.wireOp",EDGE,"E72.1");var subQ16=sQuery(id+"F12.wireOp",EDGE,"E74.1");var subQ18=sQuery(id+"F12.wireOp",EDGE,"E74.8");Q0=qUnion([makeQuery(id+"F12.imprint","IMPRINT",FACE,{"disambiguationData":[TD([[makeQuery(id+"F12.imprint","IMPRINT",EDGE,{"derivedFrom":subQ7}),1.0]])]}),makeQuery(id+"F12.imprint","IMPRINT",FACE,{"disambiguationData":[TD([[makeQuery(id+"F12.imprint","IMPRINT",EDGE,{"derivedFrom":subQ14}),1.0]])]}),makeQuery(id+"F12.imprint","IMPRINT",FACE,{"disambiguationData":[TD([[makeQuery(id+"F12.imprint","IMPRINT",EDGE,{"derivedFrom":subQ16}),1.0]])]}),makeQuery(id+"F12.imprint","IMPRINT",FACE,{"disambiguationData":[TD([[makeQuery(id+"F12.imprint","IMPRINT",EDGE,{"derivedFrom":subQ18}),-1.0]])]})]);}
            var Q1;
            Q1=makeQuery(id+"F5.boolean.opBoolean","SPLIT",FACE,{"disambiguationData":[TD([makeQuery(id+"F5.opExtrude","SWEPT_FACE",FACE,{"disambiguationData":[OSD([sQuery(id+"F4.wireOp",EDGE,"E41")])]})])],"derivedFrom":makeQuery(id+"F3.boolean.opBoolean","COPY",FACE,{"derivedFrom":makeQuery(id+"F3.opExtrude","CAP_FACE",FACE,{"disambiguationData":[OSD([sQuery(id+"F0.wireOp",EDGE,"E25.0"),sQuery(id+"F0.wireOp",EDGE,"E25.1"),sQuery(id+"F0.wireOp",EDGE,"E25.2"),sQuery(id+"F0.wireOp",EDGE,"E25.3"),sQuery(id+"F0.wireOp",EDGE,"E25.4"),sQuery(id+"F0.wireOp",EDGE,"E25.5"),sQuery(id+"F0.wireOp",EDGE,"E25.6"),sQuery(id+"F0.wireOp",EDGE,"E25.7")])],"isStart":false})})});
            extrude(context, id + "F13", {"entities" : qUnion([Q0]), "operationType" : NewBodyOperationType.REMOVE, "endBound" : BoundingType.UP_TO_SURFACE, "endBoundEntityFace" : qUnion([Q1]), "depth" : 25 * mm});
        }
        {
            var Q0;
            Q0=makeQuery(id+"F3.boolean.opBoolean","COPY",EDGE,{"derivedFrom":makeQuery(id+"F3.opExtrude","CAP_EDGE",EDGE,{"disambiguationData":[OSD([sQuery(id+"F0.wireOp",EDGE,"E25.6")])],"isStart":false})});
            var Q1;
            Q1=makeQuery(id+"F8.boolean.opBoolean","INTERSECT",EDGE,{"derivedFrom":[makeQuery(id+"F5.opExtrude","SWEPT_FACE",FACE,{"disambiguationData":[OSD([sQuery(id+"F4.wireOp",EDGE,"E30")])]}),makeQuery(id+"F8.opExtrude","CAP_FACE",FACE,{"disambiguationData":[OSD([sQuery(id+"F7.wireOp",EDGE,"E67")])],"isStart":false})]});
            var Q2;
            Q2=makeQuery(id+"F8.boolean.opBoolean","INTERSECT",EDGE,{"disambiguationData":[OD(1.0)],"derivedFrom":[makeQuery(id+"F5.opExtrude","SWEPT_FACE",FACE,{"disambiguationData":[OSD([sQuery(id+"F4.wireOp",EDGE,"E30")])]}),makeQuery(id+"F8.opExtrude","SWEPT_FACE",FACE,{"disambiguationData":[OSD([sQuery(id+"F7.wireOp",EDGE,"E67")])]})]});
            var Q3;
            {var subQ0=sQuery(id+"F4.wireOp",EDGE,"E30");Q3=makeQuery(id+"F8.boolean.opBoolean","SPLIT",EDGE,{"disambiguationData":[TD([makeQuery(id+"F5.opExtrude","SWEPT_FACE",FACE,{"disambiguationData":[OSD([sQuery(id+"F4.wireOp",EDGE,"E35.filletArc")])]})])],"derivedFrom":makeQuery(id+"F5.opExtrude","CAP_EDGE",EDGE,{"disambiguationData":[OSD([subQ0])],"isStart":false})});}
            var Q4;
            {var subQ0=sQuery(id+"F0.wireOp",EDGE,"E25.7");var subQ1=sQuery(id+"F0.wireOp",EDGE,"E25.1");var subQ2=sQuery(id+"F0.wireOp",EDGE,"E25.6");var subQ3=sQuery(id+"F0.wireOp",EDGE,"E25.5");var subQ4=sQuery(id+"F0.wireOp",EDGE,"E25.4");var subQ5=sQuery(id+"F0.wireOp",EDGE,"E25.0");var subQ6=sQuery(id+"F0.wireOp",EDGE,"E25.2");var subQ7=sQuery(id+"F0.wireOp",EDGE,"E25.3");Q4=makeQuery(id+"F8.boolean.opBoolean","INTERSECT",EDGE,{"derivedFrom":[makeQuery(id+"F5.boolean.opBoolean","SPLIT",FACE,{"disambiguationData":[TD([makeQuery(id+"F2.opExtrude","SWEPT_FACE",FACE,{"disambiguationData":[OSD([subQ5])]})])],"derivedFrom":makeQuery(id+"F3.boolean.opBoolean","COPY",FACE,{"derivedFrom":makeQuery(id+"F3.opExtrude","CAP_FACE",FACE,{"disambiguationData":[OSD([subQ5,subQ1,subQ6,subQ7,subQ4,subQ3,subQ2,subQ0])],"isStart":false})})}),makeQuery(id+"F8.opExtrude","SWEPT_FACE",FACE,{"disambiguationData":[OSD([sQuery(id+"F7.wireOp",EDGE,"E67")])]})]});}
            var Q5;
            Q5=makeQuery(id+"F8.boolean.opBoolean","INTERSECT",EDGE,{"disambiguationData":[OD(0.0)],"derivedFrom":[makeQuery(id+"F5.opExtrude","SWEPT_FACE",FACE,{"disambiguationData":[OSD([sQuery(id+"F4.wireOp",EDGE,"E30")])]}),makeQuery(id+"F8.opExtrude","SWEPT_FACE",FACE,{"disambiguationData":[OSD([sQuery(id+"F7.wireOp",EDGE,"E67")])]})]});
            fillet(context, id + "F14", {"entities" : qUnion([Q0, Q1, Q2, Q3, Q4, Q5]), "radius" : 3 * mm, "tangentPropagation" : true, "allowEdgeOverflow" : false});
        }
        {
            var Q0;
            Q0=makeQuery(id+"F1.opExtrude","CAP_EDGE",EDGE,{"disambiguationData":[OSD([sQuery(id+"F0.wireOp",EDGE,"E1.bottom")])],"isStart":false});
            fillet(context, id + "F15", {"entities" : qUnion([Q0]), "radius" : 2 * mm, "tangentPropagation" : true, "allowEdgeOverflow" : false});
        }
        {
            var Q0;
            {var subQ0=sQuery(id+"F0.wireOp",EDGE,"E21.filletArc");var subQ1=sQuery(id+"F0.wireOp",EDGE,"E7");var subQ2=sQuery(id+"F0.wireOp",EDGE,"E6");var subQ3=sQuery(id+"F0.wireOp",EDGE,"E5");var subQ4=sQuery(id+"F0.wireOp",EDGE,"E4");var subQ5=sQuery(id+"F0.wireOp",EDGE,"E22.filletArc");var subQ6=sQuery(id+"F0.wireOp",EDGE,"E1.bottom");var subQ7=sQuery(id+"F0.wireOp",EDGE,"E1.right");var subQ8=sQuery(id+"F0.wireOp",EDGE,"E1.top");var subQ9=sQuery(id+"F0.wireOp",EDGE,"E1.left");var subQ10=sQuery(id+"F0.wireOp",EDGE,"E23.filletArc");var subQ11=sQuery(id+"F0.wireOp",EDGE,"E24.filletArc");Q0=makeQuery(id+"F2.boolean.opBoolean","SPLIT",FACE,{"disambiguationData":[TD([makeQuery(id+"F1.opExtrude","SWEPT_FACE",FACE,{"disambiguationData":[OSD([subQ6])]})])],"derivedFrom":makeQuery(id+"F1.opExtrude","CAP_FACE",FACE,{"disambiguationData":[OSD([subQ6,subQ8,subQ9,subQ7,subQ4,subQ3,subQ2,subQ1,subQ0,subQ5,subQ10,subQ11])],"isStart":true})});}
            var sketch = newSketch(context, id + "F16", { "sketchPlane" : qUnion([Q0])});
            skLineSegment(sketch, "E79", {"start": v(0, 90) * mm, "end": v(0, 120) * mm, "construction": true});
            skCircle(sketch, "E80", {"center": v(0, 120) * mm, "radius": 6 * mm});
            skArc(sketch, "E81", {"start": v(15, 120) * mm, "mid": v(0, 135) * mm, "end": v(-15, 120) * mm});
            skLineSegment(sketch, "E82", {"start": v(-15, 120) * mm, "end": v(-15, 108) * mm});
            skLineSegment(sketch, "E83", {"start": v(15, 120) * mm, "end": v(15, 108) * mm});
            skLineSegment(sketch, "E84", {"start": v(15, 108) * mm, "end": v(33, 90) * mm});
            skLineSegment(sketch, "E85", {"start": v(-15, 108) * mm, "end": v(-33, 90) * mm});
            skLineSegment(sketch, "E86", {"start": v(-80, 0) * mm, "end": v(80, 0) * mm, "construction": true});
            skLineSegment(sketch, "E87.MirrorCS", {"start": v(15, -120) * mm, "end": v(15, -108) * mm});
            skLineSegment(sketch, "E88.MirrorCS", {"start": v(-15, -120) * mm, "end": v(-15, -108) * mm});
            skCircle(sketch, "E89.MirrorC", {"center": v(0, -120) * mm, "radius": 6 * mm});
            skLineSegment(sketch, "E90.MirrorCS", {"start": v(15, -108) * mm, "end": v(33, -90) * mm});
            skArc(sketch, "E91.MirrorCS", {"start": v(15, -120) * mm, "mid": v(0, -135) * mm, "end": v(-15, -120) * mm});
            skLineSegment(sketch, "E92.MirrorCS", {"start": v(0, -90) * mm, "end": v(0, -120) * mm, "construction": true});
            skLineSegment(sketch, "E93.MirrorCS", {"start": v(-15, -108) * mm, "end": v(-33, -90) * mm});
            skSolve(sketch);
        }
        {
            var Q0;
            Q0=makeQuery(id+"F16.imprint","IMPRINT",FACE,{"disambiguationData":[TD([[makeQuery(id+"F16.imprint","IMPRINT",EDGE,{"derivedFrom":sQuery(id+"F16.wireOp",EDGE,"E80")}),-1.0]])]});
            var Q1;
            Q1=makeQuery(id+"F16.imprint","IMPRINT",FACE,{"disambiguationData":[TD([[makeQuery(id+"F16.imprint","IMPRINT",EDGE,{"derivedFrom":makeQuery(id+"F1.opExtrude","CAP_EDGE",EDGE,{"disambiguationData":[OSD([sQuery(id+"F0.wireOp",EDGE,"E1.left")])],"isStart":true})}),-1.0]])]});
            var Q2;
            Q2=makeQuery(id+"F16.imprint","IMPRINT",FACE,{"disambiguationData":[TD([[makeQuery(id+"F16.imprint","IMPRINT",EDGE,{"derivedFrom":sQuery(id+"F16.wireOp",EDGE,"E87.MirrorCS")}),1.0]])]});
            var Q3;
            Q3=makeQuery(id+"F2.opExtrude","CAP_FACE",FACE,{"disambiguationData":[OSD([sQuery(id+"F0.wireOp",EDGE,"E12"),sQuery(id+"F0.wireOp",EDGE,"E13"),sQuery(id+"F0.wireOp",EDGE,"E14"),sQuery(id+"F0.wireOp",EDGE,"E15"),sQuery(id+"F0.wireOp",EDGE,"E17.filletArc"),sQuery(id+"F0.wireOp",EDGE,"E18.filletArc"),sQuery(id+"F0.wireOp",EDGE,"E19.filletArc"),sQuery(id+"F0.wireOp",EDGE,"E20.filletArc"),sQuery(id+"F0.wireOp",EDGE,"E25.0"),sQuery(id+"F0.wireOp",EDGE,"E25.1"),sQuery(id+"F0.wireOp",EDGE,"E25.2"),sQuery(id+"F0.wireOp",EDGE,"E25.3"),sQuery(id+"F0.wireOp",EDGE,"E25.4"),sQuery(id+"F0.wireOp",EDGE,"E25.5"),sQuery(id+"F0.wireOp",EDGE,"E25.6"),sQuery(id+"F0.wireOp",EDGE,"E25.7")])],"isStart":false});
            extrude(context, id + "F17", {"entities" : qUnion([Q0, Q1, Q2]), "endBound" : BoundingType.UP_TO_SURFACE, "endBoundEntityFace" : qUnion([Q3]), "depth" : 25 * mm});
        }
    });
